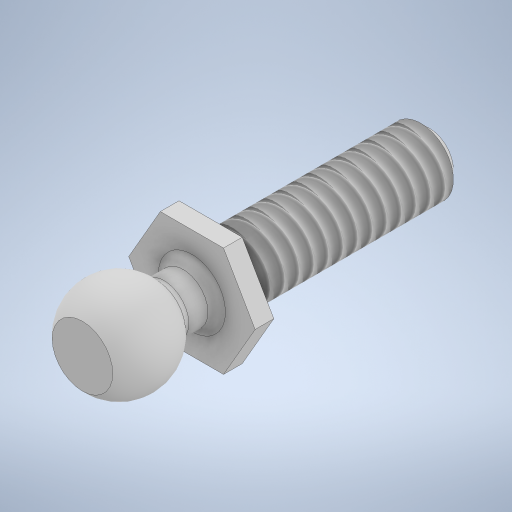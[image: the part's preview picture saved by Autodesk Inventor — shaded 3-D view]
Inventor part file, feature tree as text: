
AUTODESK INVENTOR PART (.ipt)
format: ipt  version: 2024 (Build 280153000, 153)  size: 311,808 bytes
history: native  units: in
note: dims shown in document units (in); Inventor stores cm internally (conversion verified against a paired STEP export)
features: sketch x4, extrude x3, revolve x1, fillet x1, plane x1, split x1, chamfer x1, thread x1
ambient origin geometry x8: Origin, YZ Plane, XZ Plane, XY Plane, X Axis, Y Axis, Z Axis, Center Point
bodies: Solid1 (feature_tree)
feature tree (13):
  extrude  "Extrusion1"  Depth=0.032in TaperAngle=0.0deg
  extrude  "Extrusion2"  Depth=0.125in TaperAngle=0.0deg
  revolve  "Revolution1"  Angle=90.0deg
  fillet  "Fillet1"  Radius=0.015in
  plane  "Work Plane1"
  split  "Split1"
  extrude  "Extrusion3"  Depth=0.015in
  chamfer  "Chamfer1"  Distance=0.375in
  thread  "Thread1"  [1 undecoded]
  sketch  "Sketch1"  dims[d0=0.1875in d1=0.032in d2=0.0in]
  sketch  "Sketch2"  dims[d3=0.085in d4=0.125in d5=0.0in]
  sketch  "Sketch3"  dims[d6=0.1625in d7=90.0deg d8=0.015in]
  sketch  "Sketch4"  dims[d9=0.1875in d10=0.112in d11=0.375in d12=0.0in d13=0.015in d14=0.125in d15=45.0deg d16=1.0236in d17=0.0in]
note: 1 required parameter value undecoded (feature->parameter linkage not recoverable at this tier; creation-order binding heuristic only, values carry confidence <= 0.55)
